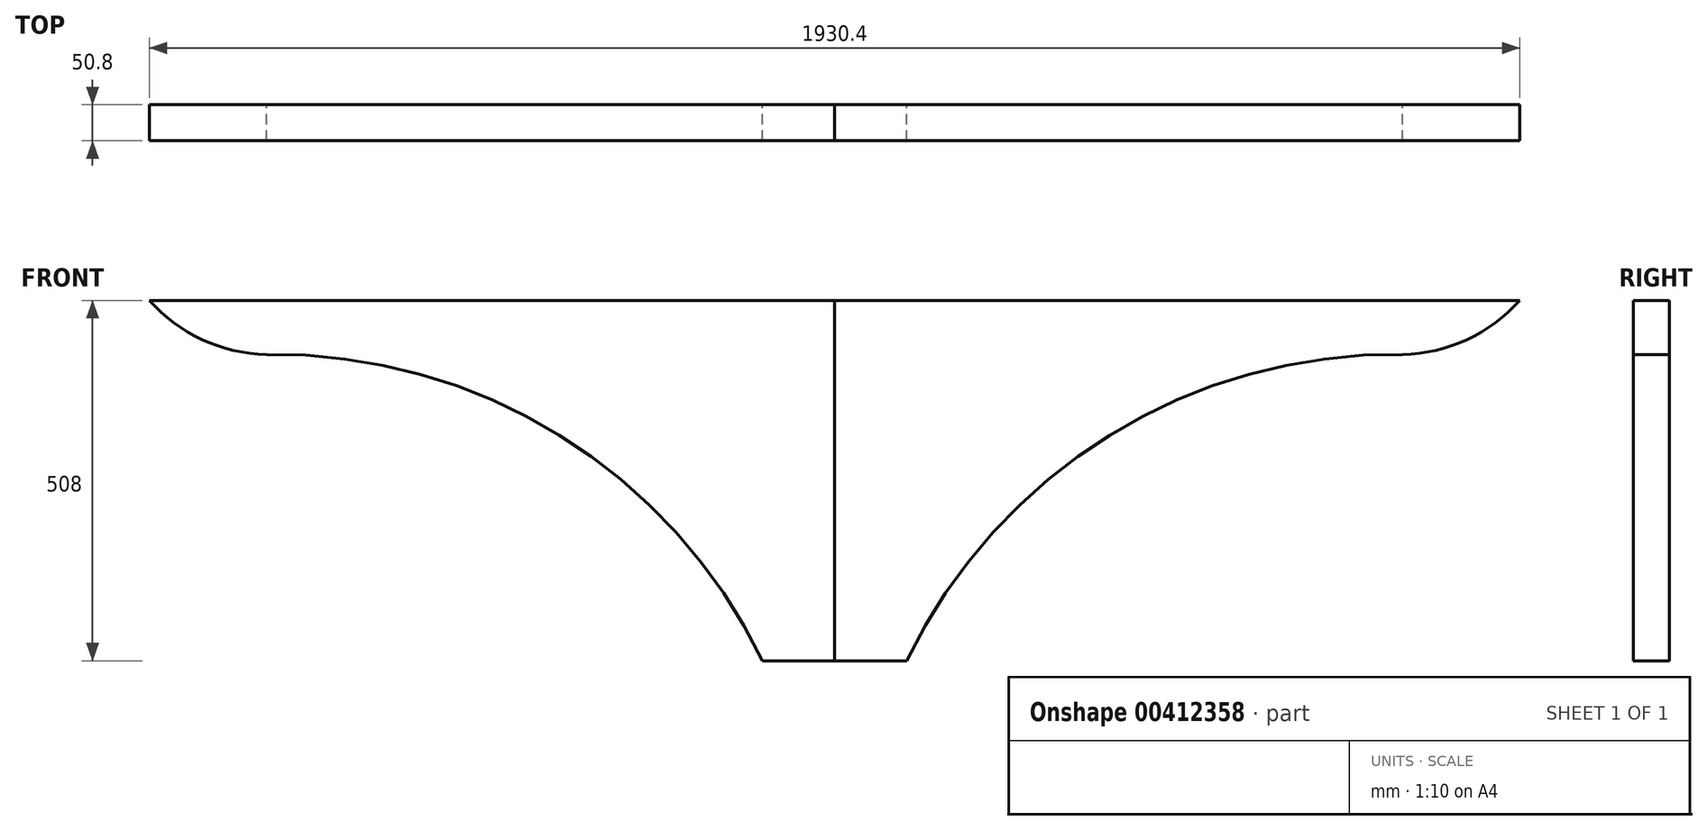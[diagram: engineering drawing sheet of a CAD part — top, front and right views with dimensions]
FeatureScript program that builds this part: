
annotation { "Feature Type Name" : "Feature", "Feature Type Description" : "" }
export const myFeature = defineFeature(function(context is Context, id is Id, definition is map)
    precondition{}
    {
        {
            var Q0;
            Q0=qCreatedBy(makeId("Front.planeOp"),FACE);
            var sketch = newSketch(context, id + "F0", { "sketchPlane" : qUnion([Q0])});
            skLineSegment(sketch, "E0", {"start": v(0, 508) * mm, "end": v(965.2, 508) * mm});
            skLineSegment(sketch, "E1", {"start": v(0, 0) * mm, "end": v(101.6, 0) * mm});
            skLineSegment(sketch, "E2", {"start": v(0, 508) * mm, "end": v(0, 0) * mm});
            skArc(sketch, "E3", {"start": v(800.1, 431.8) * mm, "mid": v(387.7, 318.04) * mm, "end": v(101.6, 0) * mm});
            skArc(sketch, "E4", {"start": v(800.1, 431.8) * mm, "mid": v(890.62, 452.64) * mm, "end": v(965.2, 508) * mm});
            skLineSegment(sketch, "E5", {"start": v(800.1, 431.8) * mm, "end": v(800.1, 508) * mm});
            skSolve(sketch);
        }
        {
            var Q0;
            Q0=makeQuery(id+"F0.imprint","IMPRINT",FACE,{"disambiguationData":[TD([[makeQuery(id+"F0.imprint","IMPRINT",EDGE,{"derivedFrom":sQuery(id+"F0.wireOp",EDGE,"E1")}),1.0]])]});
            var Q1;
            {var subQ0=sQuery(id+"F0.wireOp",EDGE,"E4");Q1=makeQuery(id+"F0.imprint","IMPRINT",FACE,{"disambiguationData":[TD([[makeQuery(id+"F0.imprint","IMPRINT",EDGE,{"derivedFrom":subQ0}),1.0]])]});}
            extrude(context, id + "F1", {"entities" : qUnion([Q0, Q1]), "depth" : 50.8 * mm});
        }
        {
            var Q0;
            Q0=makeQuery(id+"F1.opExtrude","SWEPT_BODY",BODY,{"disambiguationData":[OSD([sQuery(id+"F0.wireOp",EDGE,"E0"),sQuery(id+"F0.wireOp",EDGE,"E1"),sQuery(id+"F0.wireOp",EDGE,"E2"),sQuery(id+"F0.wireOp",EDGE,"E3"),sQuery(id+"F0.wireOp",EDGE,"E4")])]});
            var Q1;
            Q1=makeQuery(id+"F1.opExtrude","CAP_FACE",FACE,{"disambiguationData":[OSD([sQuery(id+"F0.wireOp",EDGE,"E0"),sQuery(id+"F0.wireOp",EDGE,"E1"),sQuery(id+"F0.wireOp",EDGE,"E2"),sQuery(id+"F0.wireOp",EDGE,"E3"),sQuery(id+"F0.wireOp",EDGE,"E4")])],"isStart":false});
            var Q2;
            Q2=qCreatedBy(makeId("Right.planeOp"),FACE);
            mirror(context, id + "F2", {"entities" : qUnion([Q0]), "faces" : qUnion([Q1]), "mirrorPlane" : qUnion([Q2])});
        }
    });
